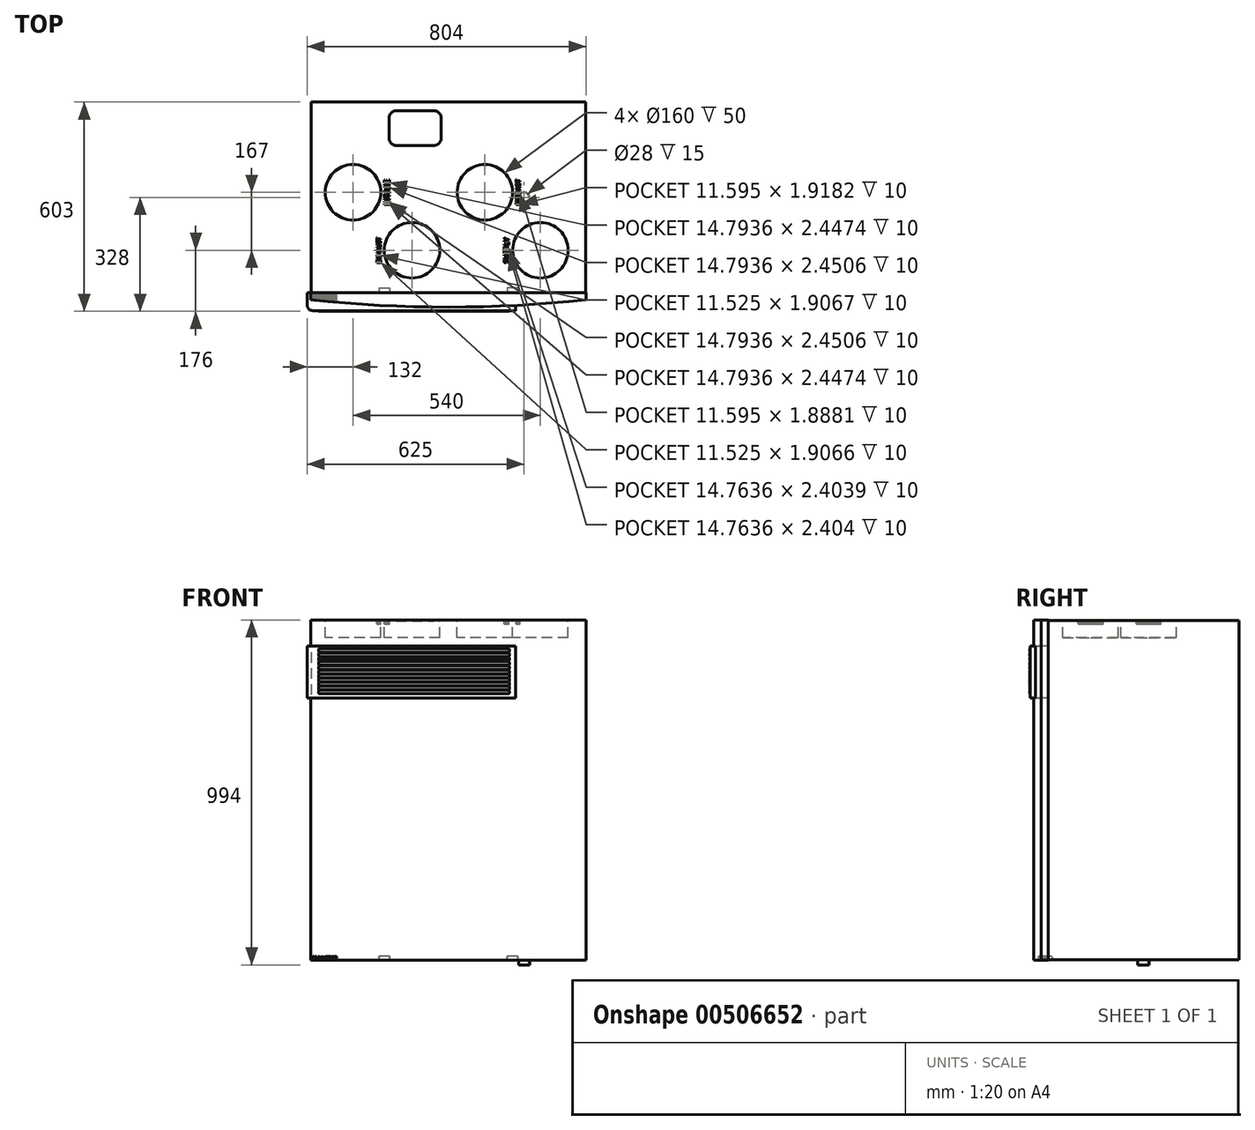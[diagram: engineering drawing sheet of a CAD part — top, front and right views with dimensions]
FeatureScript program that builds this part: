
annotation { "Feature Type Name" : "Feature", "Feature Type Description" : "" }
export const myFeature = defineFeature(function(context is Context, id is Id, definition is map)
    precondition{}
    {
        {
            var Q0;
            Q0=qCreatedBy(makeId("Top.planeOp"),FACE);
            var sketch = newSketch(context, id + "F0", { "sketchPlane" : qUnion([Q0])});
            skLineSegment(sketch, "E0", {"start": v(0, 0) * mm, "end": v(0, 275) * mm, "construction": true});
            skLineSegment(sketch, "E1", {"start": v(0, 275) * mm, "end": v(396, 275) * mm, "construction": true});
            skLineSegment(sketch, "E2.bottom", {"start": v(396, 275) * mm, "end": v(-396, 275) * mm});
            skLineSegment(sketch, "E2.top", {"start": v(396, -275) * mm, "end": v(-396, -275) * mm});
            skLineSegment(sketch, "E2.left", {"start": v(396, 275) * mm, "end": v(396, -275) * mm});
            skLineSegment(sketch, "E2.right", {"start": v(-396, 275) * mm, "end": v(-396, -275) * mm});
            skPoint(sketch, "E2.middle", {"position": v(0, 0) * mm});
            skSolve(sketch);
        }
        {
            var Q0;
            Q0 = qSketchRegion(id + "F0", true);
            extrude(context, id + "F1", {"entities" : qUnion([Q0]), "depth" : 978 * mm});
        }
        {
            var Q0;
            Q0=makeQuery(id+"F1.opExtrude","CAP_FACE",FACE,{"disambiguationData":[OSD([sQuery(id+"F0.wireOp",EDGE,"E2.bottom"),sQuery(id+"F0.wireOp",EDGE,"E2.top"),sQuery(id+"F0.wireOp",EDGE,"E2.left"),sQuery(id+"F0.wireOp",EDGE,"E2.right")])],"isStart":false});
            var sketch = newSketch(context, id + "F2", { "sketchPlane" : qUnion([Q0])});
            skLineSegment(sketch, "E3.0", {"start": v(396, -275) * mm, "end": v(-396, -275) * mm, "construction": true});
            skLineSegment(sketch, "E4", {"start": v(0, -275) * mm, "end": v(0, -316) * mm, "construction": true});
            skPoint(sketch, "E4.endSnap0", {"position": v(0, -275) * mm});
            skLineSegment(sketch, "E5", {"start": v(-396, -275) * mm, "end": v(-397, -275) * mm, "construction": true});
            skLineSegment(sketch, "E6", {"start": v(-397, -275) * mm, "end": v(-397, -295) * mm});
            skLineSegment(sketch, "E7", {"start": v(0, -316) * mm, "end": v(-397, -295) * mm, "construction": true});
            skLineSegment(sketch, "E8", {"start": v(-198.5, -305.5) * mm, "end": v(0, 3447.1) * mm, "construction": true});
            skLineSegment(sketch, "E9", {"start": v(0, -316) * mm, "end": v(0, 3447.1) * mm, "construction": true});
            skArc(sketch, "E10", {"start": v(-397, -295) * mm, "mid": v(0, -316) * mm, "end": v(397, -295) * mm});
            skLineSegment(sketch, "E11.MirrorCS", {"start": v(397, -275) * mm, "end": v(397, -295) * mm});
            skLineSegment(sketch, "E12.MirrorCS", {"start": v(396, -275) * mm, "end": v(397, -275) * mm, "construction": true});
            skLineSegment(sketch, "E13", {"start": v(-397, -275) * mm, "end": v(397, -275) * mm});
            skSolve(sketch);
        }
        {
            var Q0;
            {var subQ2=sQuery(id+"F2.wireOp",EDGE,"E6");Q0=makeQuery(id+"F2.imprint","IMPRINT",FACE,{"disambiguationData":[TD([[makeQuery(id+"F2.imprint","IMPRINT",EDGE,{"derivedFrom":subQ2}),1.0]])]});}
            var Q1;
            Q1=makeQuery(id+"F1.opExtrude","CAP_FACE",FACE,{"disambiguationData":[OSD([sQuery(id+"F0.wireOp",EDGE,"E2.bottom"),sQuery(id+"F0.wireOp",EDGE,"E2.top"),sQuery(id+"F0.wireOp",EDGE,"E2.left"),sQuery(id+"F0.wireOp",EDGE,"E2.right")])],"isStart":true});
            extrude(context, id + "F3", {"entities" : qUnion([Q0]), "operationType" : NewBodyOperationType.ADD, "endBound" : BoundingType.UP_TO_SURFACE, "oppositeDirection" : true, "endBoundEntityFace" : qUnion([Q1]), "depth" : 25 * mm, "hasSecondDirection" : true, "secondDirectionOppositeDirection" : false, "secondDirectionDepth" : 1 * mm});
        }
        {
            var Q0;
            Q0=makeQuery(id+"F1.opExtrude","CAP_FACE",FACE,{"disambiguationData":[OSD([sQuery(id+"F0.wireOp",EDGE,"E2.bottom"),sQuery(id+"F0.wireOp",EDGE,"E2.top"),sQuery(id+"F0.wireOp",EDGE,"E2.left"),sQuery(id+"F0.wireOp",EDGE,"E2.right")])],"isStart":false});
            var sketch = newSketch(context, id + "F4", { "sketchPlane" : qUnion([Q0])});
            skLineSegment(sketch, "E14", {"start": v(-396, 275) * mm, "end": v(-105, 275) * mm, "construction": true});
            skLineSegment(sketch, "E15", {"start": v(-105, 275) * mm, "end": v(-105, -152) * mm, "construction": true});
            skLineSegment(sketch, "E16", {"start": v(-396, 275) * mm, "end": v(-275, 275) * mm, "construction": true});
            skLineSegment(sketch, "E17", {"start": v(-275, 275) * mm, "end": v(-275, 15) * mm, "construction": true});
            skCircle(sketch, "E18", {"center": v(-275, 15) * mm, "radius": 80 * mm});
            skCircle(sketch, "E19", {"center": v(-105, -152) * mm, "radius": 80 * mm});
            skLineSegment(sketch, "E20", {"start": v(396, 275) * mm, "end": v(105, 275) * mm, "construction": true});
            skLineSegment(sketch, "E21", {"start": v(105, 275) * mm, "end": v(105, 15) * mm, "construction": true});
            skLineSegment(sketch, "E22", {"start": v(396, 275) * mm, "end": v(265, 275) * mm, "construction": true});
            skLineSegment(sketch, "E23", {"start": v(265, 275) * mm, "end": v(265, -152) * mm, "construction": true});
            skCircle(sketch, "E24", {"center": v(265, -152) * mm, "radius": 80 * mm});
            skCircle(sketch, "E25", {"center": v(105, 15) * mm, "radius": 80 * mm});
            skSolve(sketch);
        }
        {
            var Q0;
            Q0 = qSketchRegion(id + "F4", true);
            extrude(context, id + "F5", {"entities" : qUnion([Q0]), "operationType" : NewBodyOperationType.REMOVE, "oppositeDirection" : true, "depth" : 50 * mm});
        }
        {
            var Q0;
            Q0=makeQuery(id+"F1.opExtrude","CAP_FACE",FACE,{"disambiguationData":[OSD([sQuery(id+"F0.wireOp",EDGE,"E2.bottom"),sQuery(id+"F0.wireOp",EDGE,"E2.top"),sQuery(id+"F0.wireOp",EDGE,"E2.left"),sQuery(id+"F0.wireOp",EDGE,"E2.right")])],"isStart":false});
            var sketch = newSketch(context, id + "F6", { "sketchPlane" : qUnion([Q0])});
            skLineSegment(sketch, "E26", {"start": v(-396, 200) * mm, "end": v(-96, 200) * mm, "construction": true});
            skLineSegment(sketch, "E27.bottom", {"start": v(-151, 250) * mm, "end": v(-41, 250) * mm});
            skLineSegment(sketch, "E27.top", {"start": v(-151, 150) * mm, "end": v(-41, 150) * mm});
            skLineSegment(sketch, "E27.left", {"start": v(-171, 230) * mm, "end": v(-171, 170) * mm});
            skLineSegment(sketch, "E27.right", {"start": v(-21, 230) * mm, "end": v(-21, 170) * mm});
            skPoint(sketch, "E27.middle", {"position": v(-96, 200) * mm});
            skPoint(sketch, "E28.visualSharp", {"position": v(-171, 250) * mm});
            skArc(sketch, "E28.filletArc", {"start": v(-151, 250) * mm, "mid": v(-165.14, 244.14) * mm, "end": v(-171, 230) * mm});
            skPoint(sketch, "E29.visualSharp", {"position": v(-21, 250) * mm});
            skArc(sketch, "E29.filletArc", {"start": v(-21, 230) * mm, "mid": v(-26.86, 244.14) * mm, "end": v(-41, 250) * mm});
            skPoint(sketch, "E30.visualSharp", {"position": v(-21, 150) * mm});
            skArc(sketch, "E30.filletArc", {"start": v(-41, 150) * mm, "mid": v(-26.86, 155.86) * mm, "end": v(-21, 170) * mm});
            skPoint(sketch, "E31.visualSharp", {"position": v(-171, 150) * mm});
            skArc(sketch, "E31.filletArc", {"start": v(-171, 170) * mm, "mid": v(-165.14, 155.86) * mm, "end": v(-151, 150) * mm});
            skSolve(sketch);
        }
        {
            var Q0;
            Q0 = qSketchRegion(id + "F6", true);
            var Q1;
            Q1 = qConstructionFilter(qBodyType(qCreatedBy(id + "F6" ,EDGE), BodyType.WIRE), ConstructionObject.NO);
            extrude(context, id + "F7", {"entities" : qUnion([Q0]), "operationType" : NewBodyOperationType.REMOVE, "surfaceEntities" : qUnion([Q1]), "oppositeDirection" : true, "depth" : 2 * mm});
        }
        {
            var Q0;
            Q0=makeQuery(id+"F3.opExtrude","CAP_EDGE",EDGE,{"disambiguationData":[OSD([sQuery(id+"F2.wireOp",EDGE,"E10")])],"isStart":true});
            cPoint(context, id + "F8", {"entities" : qUnion([Q0]), "parameter" : 0.5});
        }
        {
            var Q0;
            Q0=qCreatedBy(makeId("Front.planeOp"),FACE);
            var Q1;
            Q1 = qCreatedBy(id + "F8" ,VERTEX);
            cPlane(context, id + "F9", {"entities" : qUnion([Q0, Q1]), "cplaneType" : CPlaneType.PLANE_POINT, "offset" : 200 * mm, "oppositeDirection" : true, "width" : 150 * mm, "height" : 150 * mm});
        }
        {
            var Q0;
            Q0=qCreatedBy(id+"F9.planeOp",FACE);
            cPlane(context, id + "F10", {"entities" : qUnion([Q0]), "cplaneType" : CPlaneType.OFFSET, "offset" : 10 * mm, "width" : 150 * mm, "height" : 150 * mm});
        }
        {
            var Q0;
            Q0=qCreatedBy(id+"F10.planeOp",FACE);
            var sketch = newSketch(context, id + "F11", { "sketchPlane" : qUnion([Q0])});
            skLineSegment(sketch, "E32.0", {"start": v(-397, 979) * mm, "end": v(397, 979) * mm, "construction": true});
            skLineSegment(sketch, "E33.bottom", {"start": v(-407, 904) * mm, "end": v(193, 904) * mm});
            skLineSegment(sketch, "E33.top", {"start": v(-407, 754) * mm, "end": v(193, 754) * mm});
            skLineSegment(sketch, "E33.left", {"start": v(-407, 904) * mm, "end": v(-407, 754) * mm});
            skLineSegment(sketch, "E33.right", {"start": v(193, 904) * mm, "end": v(193, 754) * mm});
            skLineSegment(sketch, "E34", {"start": v(-397, 979) * mm, "end": v(-407, 979) * mm});
            skLineSegment(sketch, "E35", {"start": v(-407, 979) * mm, "end": v(-407, 904) * mm, "construction": true});
            skSolve(sketch);
        }
        {
            var Q0;
            Q0=makeQuery(id+"F11.imprint","IMPRINT",FACE,{"disambiguationData":[TD([[makeQuery(id+"F11.imprint","IMPRINT",EDGE,{"derivedFrom":sQuery(id+"F11.wireOp",EDGE,"E33.bottom")}),-1.0]])]});
            var Q1;
            Q1=makeQuery(id+"F3.opExtrude","SWEPT_FACE",FACE,{"disambiguationData":[OSD([sQuery(id+"F2.wireOp",EDGE,"E13")])]});
            extrude(context, id + "F12", {"entities" : qUnion([Q0]), "operationType" : NewBodyOperationType.ADD, "endBound" : BoundingType.UP_TO_SURFACE, "oppositeDirection" : true, "endBoundEntityFace" : qUnion([Q1]), "depth" : 25 * mm});
        }
        {
            var Q0;
            Q0=makeQuery(id+"F12.opExtrude","CAP_EDGE",EDGE,{"disambiguationData":[OSD([sQuery(id+"F11.wireOp",EDGE,"E33.left")])],"isStart":true});
            fillet(context, id + "F13", {"entities" : qUnion([Q0]), "radius" : 15 * mm, "tangentPropagation" : true, "allowEdgeOverflow" : false});
        }
        {
            var Q0;
            Q0=makeQuery(id+"F1.opExtrude","CAP_FACE",FACE,{"disambiguationData":[OSD([sQuery(id+"F0.wireOp",EDGE,"E2.bottom"),sQuery(id+"F0.wireOp",EDGE,"E2.top"),sQuery(id+"F0.wireOp",EDGE,"E2.left"),sQuery(id+"F0.wireOp",EDGE,"E2.right")])],"isStart":false});
            var sketch = newSketch(context, id + "F14", { "sketchPlane" : qUnion([Q0])});
            skCircle(sketch, "E36.0", {"center": v(105, 15) * mm, "radius": 80 * mm, "construction": true});
            skCircle(sketch, "E36.1", {"center": v(265, -152) * mm, "radius": 80 * mm, "construction": true});
            skCircle(sketch, "E36.2", {"center": v(-105, -152) * mm, "radius": 80 * mm, "construction": true});
            skCircle(sketch, "E36.3", {"center": v(-275, 15) * mm, "radius": 80 * mm, "construction": true});
            skLineSegment(sketch, "E37", {"start": v(105, 15) * mm, "end": v(195, 15) * mm, "construction": true});
            skText(sketch, "E38", { "text": "EXTRACT", "fontName": "AllertaStencil-Regular.ttf"});
            skLineSegment(sketch, "E39", {"start": v(265, -152) * mm, "end": v(175, -152) * mm, "construction": true});
            skText(sketch, "E40", { "text": "SUPPLY", "fontName": "AllertaStencil-Regular.ttf"});
            skLineSegment(sketch, "E41", {"start": v(-105, -152) * mm, "end": v(-195, -152) * mm, "construction": true});
            skText(sketch, "E42", { "text": "EXHAUST", "fontName": "AllertaStencil-Regular.ttf"});
            skLineSegment(sketch, "E43", {"start": v(-275, 15) * mm, "end": v(-185, 15) * mm, "construction": true});
            skText(sketch, "E44", { "text": "INTAKE ", "fontName": "AllertaStencil-Regular.ttf"});
            const initialGuessF14  = {"E38": [0.2066, -0.0225, 0, 1, 0.0116], "E40": [0.175, -0.1895, 0, 1, 0.01477], "E42": [-0.195, -0.1895, 0, 1, 0.01153], "E44": [-0.1702, -0.0225, 0, 1, 0.0148]};
            skSetInitialGuess(sketch, initialGuessF14);
            skSolve(sketch);
        }
        {
            var Q0;
            Q0 = qSketchRegion(id + "F14", true);
            extrude(context, id + "F15", {"entities" : qUnion([Q0]), "operationType" : NewBodyOperationType.REMOVE, "oppositeDirection" : true, "depth" : 10 * mm});
        }
        {
            var Q0;
            Q0=makeQuery(id+"F12.opExtrude","CAP_FACE",FACE,{"disambiguationData":[OSD([sQuery(id+"F11.wireOp",EDGE,"E33.bottom"),sQuery(id+"F11.wireOp",EDGE,"E33.top"),sQuery(id+"F11.wireOp",EDGE,"E33.left"),sQuery(id+"F11.wireOp",EDGE,"E33.right")])],"isStart":true});
            var sketch = newSketch(context, id + "F16", { "sketchPlane" : qUnion([Q0])});
            skLineSegment(sketch, "E45", {"start": v(193, 829) * mm, "end": v(-392, 829) * mm, "construction": true});
            skLineSegment(sketch, "E46.bottom", {"start": v(-372, 834) * mm, "end": v(173, 834) * mm});
            skLineSegment(sketch, "E46.top", {"start": v(-372, 824) * mm, "end": v(173, 824) * mm});
            skLineSegment(sketch, "E46.left", {"start": v(-374.5, 831.5) * mm, "end": v(-374.5, 826.5) * mm});
            skLineSegment(sketch, "E46.right", {"start": v(175.5, 831.5) * mm, "end": v(175.5, 826.5) * mm});
            skPoint(sketch, "E46.middle", {"position": v(-99.5, 829) * mm});
            skPoint(sketch, "E47.visualSharp", {"position": v(-374.5, 834) * mm});
            skArc(sketch, "E47.filletArc", {"start": v(-372, 834) * mm, "mid": v(-373.77, 833.27) * mm, "end": v(-374.5, 831.5) * mm});
            skPoint(sketch, "E48.visualSharp", {"position": v(-374.5, 824) * mm});
            skArc(sketch, "E48.filletArc", {"start": v(-374.5, 826.5) * mm, "mid": v(-373.77, 824.73) * mm, "end": v(-372, 824) * mm});
            skPoint(sketch, "E49.visualSharp", {"position": v(175.5, 824) * mm});
            skArc(sketch, "E49.filletArc", {"start": v(173, 824) * mm, "mid": v(174.77, 824.73) * mm, "end": v(175.5, 826.5) * mm});
            skPoint(sketch, "E50.visualSharp", {"position": v(175.5, 834) * mm});
            skArc(sketch, "E50.filletArc", {"start": v(175.5, 831.5) * mm, "mid": v(174.77, 833.27) * mm, "end": v(173, 834) * mm});
            skArc(sketch, "E51.0.1.0", {"start": v(-374.5, 839) * mm, "mid": v(-373.77, 837.23) * mm, "end": v(-372, 836.5) * mm});
            skLineSegment(sketch, "E51.0.1.1", {"start": v(-374.5, 844) * mm, "end": v(-374.5, 839) * mm});
            skArc(sketch, "E51.0.1.2", {"start": v(-372, 846.5) * mm, "mid": v(-373.77, 845.77) * mm, "end": v(-374.5, 844) * mm});
            skLineSegment(sketch, "E51.0.1.3", {"start": v(-372, 846.5) * mm, "end": v(173, 846.5) * mm});
            skLineSegment(sketch, "E51.0.1.4", {"start": v(-372, 836.5) * mm, "end": v(173, 836.5) * mm});
            skArc(sketch, "E51.0.1.5", {"start": v(173, 836.5) * mm, "mid": v(174.77, 837.23) * mm, "end": v(175.5, 839) * mm});
            skLineSegment(sketch, "E51.0.1.6", {"start": v(175.5, 844) * mm, "end": v(175.5, 839) * mm});
            skArc(sketch, "E51.0.1.7", {"start": v(175.5, 844) * mm, "mid": v(174.77, 845.77) * mm, "end": v(173, 846.5) * mm});
            skArc(sketch, "E51.0.2.0", {"start": v(-374.5, 851.5) * mm, "mid": v(-373.77, 849.73) * mm, "end": v(-372, 849) * mm});
            skLineSegment(sketch, "E51.0.2.1", {"start": v(-374.5, 856.5) * mm, "end": v(-374.5, 851.5) * mm});
            skArc(sketch, "E51.0.2.2", {"start": v(-372, 859) * mm, "mid": v(-373.77, 858.27) * mm, "end": v(-374.5, 856.5) * mm});
            skLineSegment(sketch, "E51.0.2.3", {"start": v(-372, 859) * mm, "end": v(173, 859) * mm});
            skLineSegment(sketch, "E51.0.2.4", {"start": v(-372, 849) * mm, "end": v(173, 849) * mm});
            skArc(sketch, "E51.0.2.5", {"start": v(173, 849) * mm, "mid": v(174.77, 849.73) * mm, "end": v(175.5, 851.5) * mm});
            skLineSegment(sketch, "E51.0.2.6", {"start": v(175.5, 856.5) * mm, "end": v(175.5, 851.5) * mm});
            skArc(sketch, "E51.0.2.7", {"start": v(175.5, 856.5) * mm, "mid": v(174.77, 858.27) * mm, "end": v(173, 859) * mm});
            skArc(sketch, "E51.0.3.0", {"start": v(-374.5, 864) * mm, "mid": v(-373.77, 862.23) * mm, "end": v(-372, 861.5) * mm});
            skLineSegment(sketch, "E51.0.3.1", {"start": v(-374.5, 869) * mm, "end": v(-374.5, 864) * mm});
            skArc(sketch, "E51.0.3.2", {"start": v(-372, 871.5) * mm, "mid": v(-373.77, 870.77) * mm, "end": v(-374.5, 869) * mm});
            skLineSegment(sketch, "E51.0.3.3", {"start": v(-372, 871.5) * mm, "end": v(173, 871.5) * mm});
            skLineSegment(sketch, "E51.0.3.4", {"start": v(-372, 861.5) * mm, "end": v(173, 861.5) * mm});
            skArc(sketch, "E51.0.3.5", {"start": v(173, 861.5) * mm, "mid": v(174.77, 862.23) * mm, "end": v(175.5, 864) * mm});
            skLineSegment(sketch, "E51.0.3.6", {"start": v(175.5, 869) * mm, "end": v(175.5, 864) * mm});
            skArc(sketch, "E51.0.3.7", {"start": v(175.5, 869) * mm, "mid": v(174.77, 870.77) * mm, "end": v(173, 871.5) * mm});
            skArc(sketch, "E51.0.4.0", {"start": v(-374.5, 876.5) * mm, "mid": v(-373.77, 874.73) * mm, "end": v(-372, 874) * mm});
            skLineSegment(sketch, "E51.0.4.1", {"start": v(-374.5, 881.5) * mm, "end": v(-374.5, 876.5) * mm});
            skArc(sketch, "E51.0.4.2", {"start": v(-372, 884) * mm, "mid": v(-373.77, 883.27) * mm, "end": v(-374.5, 881.5) * mm});
            skLineSegment(sketch, "E51.0.4.3", {"start": v(-372, 884) * mm, "end": v(173, 884) * mm});
            skLineSegment(sketch, "E51.0.4.4", {"start": v(-372, 874) * mm, "end": v(173, 874) * mm});
            skArc(sketch, "E51.0.4.5", {"start": v(173, 874) * mm, "mid": v(174.77, 874.73) * mm, "end": v(175.5, 876.5) * mm});
            skLineSegment(sketch, "E51.0.4.6", {"start": v(175.5, 881.5) * mm, "end": v(175.5, 876.5) * mm});
            skArc(sketch, "E51.0.4.7", {"start": v(175.5, 881.5) * mm, "mid": v(174.77, 883.27) * mm, "end": v(173, 884) * mm});
            skArc(sketch, "E51.0.5.0", {"start": v(-374.5, 889) * mm, "mid": v(-373.77, 887.23) * mm, "end": v(-372, 886.5) * mm});
            skLineSegment(sketch, "E51.0.5.1", {"start": v(-374.5, 894) * mm, "end": v(-374.5, 889) * mm});
            skArc(sketch, "E51.0.5.2", {"start": v(-372, 896.5) * mm, "mid": v(-373.77, 895.77) * mm, "end": v(-374.5, 894) * mm});
            skLineSegment(sketch, "E51.0.5.3", {"start": v(-372, 896.5) * mm, "end": v(173, 896.5) * mm});
            skLineSegment(sketch, "E51.0.5.4", {"start": v(-372, 886.5) * mm, "end": v(173, 886.5) * mm});
            skArc(sketch, "E51.0.5.5", {"start": v(173, 886.5) * mm, "mid": v(174.77, 887.23) * mm, "end": v(175.5, 889) * mm});
            skLineSegment(sketch, "E51.0.5.6", {"start": v(175.5, 894) * mm, "end": v(175.5, 889) * mm});
            skArc(sketch, "E51.0.5.7", {"start": v(175.5, 894) * mm, "mid": v(174.77, 895.77) * mm, "end": v(173, 896.5) * mm});
            skLineSegment(sketch, "E51.direction1", {"start": v(-372, 824) * mm, "end": v(-362.5, 824) * mm, "construction": true});
            skLineSegment(sketch, "E51.direction2", {"start": v(-372, 824) * mm, "end": v(-372, 836.5) * mm, "construction": true});
            skSolve(sketch);
        }
        {
            var Q0;
            Q0=makeQuery(id+"F16.imprint","IMPRINT",FACE,{"disambiguationData":[TD([[makeQuery(id+"F16.imprint","IMPRINT",EDGE,{"derivedFrom":sQuery(id+"F16.wireOp",EDGE,"E46.bottom")}),-1.0]])]});
            var Q1;
            Q1=makeQuery(id+"F16.imprint","IMPRINT",FACE,{"disambiguationData":[TD([[makeQuery(id+"F16.imprint","IMPRINT",EDGE,{"derivedFrom":sQuery(id+"F16.wireOp",EDGE,"E51.0.1.0")}),1.0]])]});
            var Q2;
            Q2=makeQuery(id+"F16.imprint","IMPRINT",FACE,{"disambiguationData":[TD([[makeQuery(id+"F16.imprint","IMPRINT",EDGE,{"derivedFrom":sQuery(id+"F16.wireOp",EDGE,"E51.0.2.0")}),1.0]])]});
            var Q3;
            Q3=makeQuery(id+"F16.imprint","IMPRINT",FACE,{"disambiguationData":[TD([[makeQuery(id+"F16.imprint","IMPRINT",EDGE,{"derivedFrom":sQuery(id+"F16.wireOp",EDGE,"E51.0.3.0")}),1.0]])]});
            var Q4;
            Q4=makeQuery(id+"F16.imprint","IMPRINT",FACE,{"disambiguationData":[TD([[makeQuery(id+"F16.imprint","IMPRINT",EDGE,{"derivedFrom":sQuery(id+"F16.wireOp",EDGE,"E51.0.4.0")}),1.0]])]});
            var Q5;
            Q5=makeQuery(id+"F16.imprint","IMPRINT",FACE,{"disambiguationData":[TD([[makeQuery(id+"F16.imprint","IMPRINT",EDGE,{"derivedFrom":sQuery(id+"F16.wireOp",EDGE,"E51.0.5.0")}),1.0]])]});
            extrude(context, id + "F17", {"entities" : qUnion([Q0, Q1, Q2, Q3, Q4, Q5]), "operationType" : NewBodyOperationType.ADD, "depth" : 2 * mm});
        }
        {
            var Q0;
            Q0=makeQuery(id+"F12.opExtrude","CAP_FACE",FACE,{"disambiguationData":[OSD([sQuery(id+"F11.wireOp",EDGE,"E33.bottom"),sQuery(id+"F11.wireOp",EDGE,"E33.top"),sQuery(id+"F11.wireOp",EDGE,"E33.left"),sQuery(id+"F11.wireOp",EDGE,"E33.right")])],"isStart":true});
            var sketch = newSketch(context, id + "F18", { "sketchPlane" : qUnion([Q0])});
            skArc(sketch, "E52.0.0", {"start": v(-374.5, 826.5) * mm, "mid": v(-373.77, 824.73) * mm, "end": v(-372, 824) * mm});
            skLineSegment(sketch, "E52.0.1", {"start": v(-372, 824) * mm, "end": v(173, 824) * mm});
            skArc(sketch, "E52.0.2", {"start": v(173, 824) * mm, "mid": v(174.77, 824.73) * mm, "end": v(175.5, 826.5) * mm});
            skLineSegment(sketch, "E52.0.3", {"start": v(175.5, 826.5) * mm, "end": v(175.5, 831.5) * mm});
            skArc(sketch, "E52.0.4", {"start": v(175.5, 831.5) * mm, "mid": v(174.77, 833.27) * mm, "end": v(173, 834) * mm});
            skLineSegment(sketch, "E52.0.5", {"start": v(173, 834) * mm, "end": v(-372, 834) * mm});
            skArc(sketch, "E52.0.6", {"start": v(-372, 834) * mm, "mid": v(-373.77, 833.27) * mm, "end": v(-374.5, 831.5) * mm});
            skLineSegment(sketch, "E52.0.7", {"start": v(-374.5, 831.5) * mm, "end": v(-374.5, 826.5) * mm});
            skLineSegment(sketch, "E53.0.1.0", {"start": v(-372, 812.5) * mm, "end": v(173, 812.5) * mm});
            skArc(sketch, "E53.0.1.1", {"start": v(-374.5, 815) * mm, "mid": v(-373.77, 813.23) * mm, "end": v(-372, 812.5) * mm});
            skLineSegment(sketch, "E53.0.1.2", {"start": v(-374.5, 820) * mm, "end": v(-374.5, 815) * mm});
            skArc(sketch, "E53.0.1.3", {"start": v(-372, 822.5) * mm, "mid": v(-373.77, 821.77) * mm, "end": v(-374.5, 820) * mm});
            skLineSegment(sketch, "E53.0.1.4", {"start": v(173, 822.5) * mm, "end": v(-372, 822.5) * mm});
            skArc(sketch, "E53.0.1.5", {"start": v(173, 812.5) * mm, "mid": v(174.77, 813.23) * mm, "end": v(175.5, 815) * mm});
            skArc(sketch, "E53.0.1.6", {"start": v(175.5, 820) * mm, "mid": v(174.77, 821.77) * mm, "end": v(173, 822.5) * mm});
            skLineSegment(sketch, "E53.0.1.7", {"start": v(175.5, 815) * mm, "end": v(175.5, 820) * mm});
            skLineSegment(sketch, "E53.0.2.0", {"start": v(-372, 801) * mm, "end": v(173, 801) * mm});
            skArc(sketch, "E53.0.2.1", {"start": v(-374.5, 803.5) * mm, "mid": v(-373.77, 801.73) * mm, "end": v(-372, 801) * mm});
            skLineSegment(sketch, "E53.0.2.2", {"start": v(-374.5, 808.5) * mm, "end": v(-374.5, 803.5) * mm});
            skArc(sketch, "E53.0.2.3", {"start": v(-372, 811) * mm, "mid": v(-373.77, 810.27) * mm, "end": v(-374.5, 808.5) * mm});
            skLineSegment(sketch, "E53.0.2.4", {"start": v(173, 811) * mm, "end": v(-372, 811) * mm});
            skArc(sketch, "E53.0.2.5", {"start": v(173, 801) * mm, "mid": v(174.77, 801.73) * mm, "end": v(175.5, 803.5) * mm});
            skArc(sketch, "E53.0.2.6", {"start": v(175.5, 808.5) * mm, "mid": v(174.77, 810.27) * mm, "end": v(173, 811) * mm});
            skLineSegment(sketch, "E53.0.2.7", {"start": v(175.5, 803.5) * mm, "end": v(175.5, 808.5) * mm});
            skLineSegment(sketch, "E53.0.3.0", {"start": v(-372, 789.5) * mm, "end": v(173, 789.5) * mm});
            skArc(sketch, "E53.0.3.1", {"start": v(-374.5, 792) * mm, "mid": v(-373.77, 790.23) * mm, "end": v(-372, 789.5) * mm});
            skLineSegment(sketch, "E53.0.3.2", {"start": v(-374.5, 797) * mm, "end": v(-374.5, 792) * mm});
            skArc(sketch, "E53.0.3.3", {"start": v(-372, 799.5) * mm, "mid": v(-373.77, 798.77) * mm, "end": v(-374.5, 797) * mm});
            skLineSegment(sketch, "E53.0.3.4", {"start": v(173, 799.5) * mm, "end": v(-372, 799.5) * mm});
            skArc(sketch, "E53.0.3.5", {"start": v(173, 789.5) * mm, "mid": v(174.77, 790.23) * mm, "end": v(175.5, 792) * mm});
            skArc(sketch, "E53.0.3.6", {"start": v(175.5, 797) * mm, "mid": v(174.77, 798.77) * mm, "end": v(173, 799.5) * mm});
            skLineSegment(sketch, "E53.0.3.7", {"start": v(175.5, 792) * mm, "end": v(175.5, 797) * mm});
            skLineSegment(sketch, "E53.0.4.0", {"start": v(-372, 778) * mm, "end": v(173, 778) * mm});
            skArc(sketch, "E53.0.4.1", {"start": v(-374.5, 780.5) * mm, "mid": v(-373.77, 778.73) * mm, "end": v(-372, 778) * mm});
            skLineSegment(sketch, "E53.0.4.2", {"start": v(-374.5, 785.5) * mm, "end": v(-374.5, 780.5) * mm});
            skArc(sketch, "E53.0.4.3", {"start": v(-372, 788) * mm, "mid": v(-373.77, 787.27) * mm, "end": v(-374.5, 785.5) * mm});
            skLineSegment(sketch, "E53.0.4.4", {"start": v(173, 788) * mm, "end": v(-372, 788) * mm});
            skArc(sketch, "E53.0.4.5", {"start": v(173, 778) * mm, "mid": v(174.77, 778.73) * mm, "end": v(175.5, 780.5) * mm});
            skArc(sketch, "E53.0.4.6", {"start": v(175.5, 785.5) * mm, "mid": v(174.77, 787.27) * mm, "end": v(173, 788) * mm});
            skLineSegment(sketch, "E53.0.4.7", {"start": v(175.5, 780.5) * mm, "end": v(175.5, 785.5) * mm});
            skLineSegment(sketch, "E53.0.5.0", {"start": v(-372, 766.5) * mm, "end": v(173, 766.5) * mm});
            skArc(sketch, "E53.0.5.1", {"start": v(-374.5, 769) * mm, "mid": v(-373.77, 767.23) * mm, "end": v(-372, 766.5) * mm});
            skLineSegment(sketch, "E53.0.5.2", {"start": v(-374.5, 774) * mm, "end": v(-374.5, 769) * mm});
            skArc(sketch, "E53.0.5.3", {"start": v(-372, 776.5) * mm, "mid": v(-373.77, 775.77) * mm, "end": v(-374.5, 774) * mm});
            skLineSegment(sketch, "E53.0.5.4", {"start": v(173, 776.5) * mm, "end": v(-372, 776.5) * mm});
            skArc(sketch, "E53.0.5.5", {"start": v(173, 766.5) * mm, "mid": v(174.77, 767.23) * mm, "end": v(175.5, 769) * mm});
            skArc(sketch, "E53.0.5.6", {"start": v(175.5, 774) * mm, "mid": v(174.77, 775.77) * mm, "end": v(173, 776.5) * mm});
            skLineSegment(sketch, "E53.0.5.7", {"start": v(175.5, 769) * mm, "end": v(175.5, 774) * mm});
            skLineSegment(sketch, "E53.direction1", {"start": v(-372, 824) * mm, "end": v(-347, 824) * mm, "construction": true});
            skLineSegment(sketch, "E53.direction2", {"start": v(-372, 824) * mm, "end": v(-372, 812.5) * mm, "construction": true});
            skSolve(sketch);
        }
        {
            var Q0;
            Q0=makeQuery(id+"F18.imprint","IMPRINT",FACE,{"disambiguationData":[TD([[makeQuery(id+"F18.imprint","IMPRINT",EDGE,{"derivedFrom":sQuery(id+"F18.wireOp",EDGE,"E52.0.0")}),1.0]])]});
            var Q1;
            Q1=makeQuery(id+"F18.imprint","IMPRINT",FACE,{"disambiguationData":[TD([[makeQuery(id+"F18.imprint","IMPRINT",EDGE,{"derivedFrom":sQuery(id+"F18.wireOp",EDGE,"E53.0.1.0")}),1.0]])]});
            var Q2;
            Q2=makeQuery(id+"F18.imprint","IMPRINT",FACE,{"disambiguationData":[TD([[makeQuery(id+"F18.imprint","IMPRINT",EDGE,{"derivedFrom":sQuery(id+"F18.wireOp",EDGE,"E53.0.2.0")}),1.0]])]});
            var Q3;
            Q3=makeQuery(id+"F18.imprint","IMPRINT",FACE,{"disambiguationData":[TD([[makeQuery(id+"F18.imprint","IMPRINT",EDGE,{"derivedFrom":sQuery(id+"F18.wireOp",EDGE,"E53.0.3.0")}),1.0]])]});
            var Q4;
            Q4=makeQuery(id+"F18.imprint","IMPRINT",FACE,{"disambiguationData":[TD([[makeQuery(id+"F18.imprint","IMPRINT",EDGE,{"derivedFrom":sQuery(id+"F18.wireOp",EDGE,"E53.0.5.0")}),1.0]])]});
            var Q5;
            Q5=makeQuery(id+"F18.imprint","IMPRINT",FACE,{"disambiguationData":[TD([[makeQuery(id+"F18.imprint","IMPRINT",EDGE,{"derivedFrom":sQuery(id+"F18.wireOp",EDGE,"E53.0.4.0")}),1.0]])]});
            extrude(context, id + "F19", {"entities" : qUnion([Q0, Q1, Q2, Q3, Q4, Q5]), "operationType" : NewBodyOperationType.ADD, "depth" : 2 * mm});
        }
        {
            var Q0;
            Q0=makeQuery(id+"F17.opExtrude","CAP_EDGE",EDGE,{"disambiguationData":[OSD([sQuery(id+"F16.wireOp",EDGE,"E51.0.5.1")])],"isStart":false});
            var Q1;
            Q1=makeQuery(id+"F17.opExtrude","CAP_EDGE",EDGE,{"disambiguationData":[OSD([sQuery(id+"F16.wireOp",EDGE,"E51.0.4.1")])],"isStart":false});
            var Q2;
            Q2=makeQuery(id+"F17.opExtrude","CAP_EDGE",EDGE,{"disambiguationData":[OSD([sQuery(id+"F16.wireOp",EDGE,"E51.0.3.1")])],"isStart":false});
            var Q3;
            Q3=makeQuery(id+"F17.opExtrude","CAP_EDGE",EDGE,{"disambiguationData":[OSD([sQuery(id+"F16.wireOp",EDGE,"E51.0.2.1")])],"isStart":false});
            var Q4;
            Q4=makeQuery(id+"F17.opExtrude","CAP_EDGE",EDGE,{"disambiguationData":[OSD([sQuery(id+"F16.wireOp",EDGE,"E51.0.1.1")])],"isStart":false});
            var Q5;
            Q5=makeQuery(id+"F17.opExtrude","CAP_EDGE",EDGE,{"disambiguationData":[OSD([sQuery(id+"F16.wireOp",EDGE,"E46.left")])],"isStart":false});
            var Q6;
            Q6=makeQuery(id+"F19.opExtrude","CAP_EDGE",EDGE,{"disambiguationData":[OSD([sQuery(id+"F18.wireOp",EDGE,"E53.0.1.2")])],"isStart":false});
            var Q7;
            Q7=makeQuery(id+"F19.opExtrude","CAP_EDGE",EDGE,{"disambiguationData":[OSD([sQuery(id+"F18.wireOp",EDGE,"E53.0.2.2")])],"isStart":false});
            var Q8;
            Q8=makeQuery(id+"F19.opExtrude","CAP_EDGE",EDGE,{"disambiguationData":[OSD([sQuery(id+"F18.wireOp",EDGE,"E53.0.3.2")])],"isStart":false});
            var Q9;
            Q9=makeQuery(id+"F19.opExtrude","CAP_EDGE",EDGE,{"disambiguationData":[OSD([sQuery(id+"F18.wireOp",EDGE,"E53.0.4.2")])],"isStart":false});
            var Q10;
            Q10=makeQuery(id+"F19.opExtrude","CAP_EDGE",EDGE,{"disambiguationData":[OSD([sQuery(id+"F18.wireOp",EDGE,"E53.0.5.2")])],"isStart":false});
            fillet(context, id + "F20", {"entities" : qUnion([Q0, Q1, Q2, Q3, Q4, Q5, Q6, Q7, Q8, Q9, Q10]), "radius" : 2 * mm, "tangentPropagation" : true, "allowEdgeOverflow" : false});
        }
        {
            var Q0;
            {var subQ0=sQuery(id+"F0.wireOp",EDGE,"E2.right");var subQ1=sQuery(id+"F0.wireOp",EDGE,"E2.left");var subQ2=sQuery(id+"F0.wireOp",EDGE,"E2.top");var subQ3=sQuery(id+"F0.wireOp",EDGE,"E2.bottom");Q0=makeQuery(id+"F3.boolean.opBoolean","MERGE",FACE,{"derivedFrom":[makeQuery(id+"F1.opExtrude","CAP_FACE",FACE,{"disambiguationData":[OSD([subQ3,subQ2,subQ1,subQ0])],"isStart":true}),makeQuery(id+"F3.opExtrude","CAP_FACE",FACE,{"disambiguationData":[OSD([subQ3,subQ2,subQ1,subQ0])],"isStart":false})]});}
            var sketch = newSketch(context, id + "F21", { "sketchPlane" : qUnion([Q0])});
            skLineSegment(sketch, "E54", {"start": v(396, -275) * mm, "end": v(218, -275) * mm, "construction": true});
            skLineSegment(sketch, "E55", {"start": v(218, -275) * mm, "end": v(218, 0) * mm, "construction": true});
            skLineSegment(sketch, "E56", {"start": v(0, 0) * mm, "end": v(218, 0) * mm, "construction": true});
            skCircle(sketch, "E57", {"center": v(218, 0) * mm, "radius": 16 * mm});
            skCircle(sketch, "E58.0", {"center": v(218, 0) * mm, "radius": 14 * mm});
            skSolve(sketch);
        }
        {
            var Q0;
            Q0 = qSketchRegion(id + "F21", true);
            extrude(context, id + "F22", {"entities" : qUnion([Q0]), "operationType" : NewBodyOperationType.ADD, "depth" : 15 * mm});
        }
        {
            var Q0;
            {var subQ0=sQuery(id+"F0.wireOp",EDGE,"E2.left");var subQ1=sQuery(id+"F0.wireOp",EDGE,"E2.right");var subQ2=sQuery(id+"F0.wireOp",EDGE,"E2.bottom");var subQ4=sQuery(id+"F0.wireOp",EDGE,"E2.top");Q0=makeQuery(id+"F22.boolean.opBoolean","SPLIT",FACE,{"disambiguationData":[TD([makeQuery(id+"F1.opExtrude","SWEPT_FACE",FACE,{"disambiguationData":[OSD([subQ2])]})])],"derivedFrom":makeQuery(id+"F3.boolean.opBoolean","MERGE",FACE,{"derivedFrom":[makeQuery(id+"F1.opExtrude","CAP_FACE",FACE,{"disambiguationData":[OSD([subQ2,subQ4,subQ0,subQ1])],"isStart":true}),makeQuery(id+"F3.opExtrude","CAP_FACE",FACE,{"disambiguationData":[OSD([subQ2,subQ4,subQ0,subQ1])],"isStart":false})]})});}
            var sketch = newSketch(context, id + "F23", { "sketchPlane" : qUnion([Q0])});
            skLineSegment(sketch, "E59.0.0", {"start": v(397, 275) * mm, "end": v(-397, 275) * mm});
            skLineSegment(sketch, "E59.0.1", {"start": v(-397, 275) * mm, "end": v(-397, 295) * mm});
            skArc(sketch, "E59.0.2", {"start": v(-397, 295) * mm, "mid": v(0, 316) * mm, "end": v(397, 295) * mm});
            skLineSegment(sketch, "E59.0.3", {"start": v(397, 295) * mm, "end": v(397, 275) * mm});
            skSolve(sketch);
        }
        {
            var Q0;
            Q0 = qSketchRegion(id + "F23", true);
            extrude(context, id + "F24", {"entities" : qUnion([Q0]), "operationType" : NewBodyOperationType.ADD, "depth" : 1 * mm});
        }
        {
            var Q0;
            {var subQ0=sQuery(id+"F0.wireOp",EDGE,"E2.left");var subQ1=sQuery(id+"F0.wireOp",EDGE,"E2.right");var subQ2=sQuery(id+"F0.wireOp",EDGE,"E2.bottom");var subQ4=sQuery(id+"F0.wireOp",EDGE,"E2.top");Q0=makeQuery(id+"F22.boolean.opBoolean","SPLIT",FACE,{"disambiguationData":[TD([makeQuery(id+"F1.opExtrude","SWEPT_FACE",FACE,{"disambiguationData":[OSD([subQ2])]})])],"derivedFrom":makeQuery(id+"F3.boolean.opBoolean","MERGE",FACE,{"derivedFrom":[makeQuery(id+"F1.opExtrude","CAP_FACE",FACE,{"disambiguationData":[OSD([subQ2,subQ4,subQ0,subQ1])],"isStart":true}),makeQuery(id+"F3.opExtrude","CAP_FACE",FACE,{"disambiguationData":[OSD([subQ2,subQ4,subQ0,subQ1])],"isStart":false})]})});}
            var sketch = newSketch(context, id + "F25", { "sketchPlane" : qUnion([Q0])});
            skLineSegment(sketch, "E60", {"start": v(0, 275) * mm, "end": v(0, 260) * mm, "construction": true});
            skPoint(sketch, "E60.endSnap0", {"position": v(0, 275) * mm});
            skLineSegment(sketch, "E61", {"start": v(0, 260) * mm, "end": v(200, 260) * mm, "construction": true});
            skLineSegment(sketch, "E62.bottom", {"start": v(200, 260) * mm, "end": v(170, 260) * mm});
            skLineSegment(sketch, "E62.top", {"start": v(200, 275) * mm, "end": v(170, 275) * mm});
            skLineSegment(sketch, "E62.left", {"start": v(200, 260) * mm, "end": v(200, 275) * mm});
            skLineSegment(sketch, "E62.right", {"start": v(170, 260) * mm, "end": v(170, 275) * mm});
            skLineSegment(sketch, "E63.MirrorCS", {"start": v(-170, 260) * mm, "end": v(-170, 275) * mm});
            skLineSegment(sketch, "E64.MirrorCS", {"start": v(0, 260) * mm, "end": v(-200, 260) * mm, "construction": true});
            skLineSegment(sketch, "E65.MirrorCS", {"start": v(-200, 275) * mm, "end": v(-170, 275) * mm});
            skLineSegment(sketch, "E66.MirrorCS", {"start": v(-200, 260) * mm, "end": v(-200, 275) * mm});
            skLineSegment(sketch, "E67.MirrorCS", {"start": v(-200, 260) * mm, "end": v(-170, 260) * mm});
            skSolve(sketch);
        }
        {
            var Q0;
            Q0 = qSketchRegion(id + "F25", true);
            extrude(context, id + "F26", {"entities" : qUnion([Q0]), "operationType" : NewBodyOperationType.REMOVE, "oppositeDirection" : true, "depth" : 10 * mm});
        }
        {
            var Q0;
            Q0=makeQuery(id+"F26.boolean.opBoolean","COPY",EDGE,{"derivedFrom":makeQuery(id+"F26.opExtrude","CAP_EDGE",EDGE,{"disambiguationData":[OSD([sQuery(id+"F25.wireOp",EDGE,"E67.MirrorCS")])],"isStart":false})});
            var Q1;
            Q1=makeQuery(id+"F26.boolean.opBoolean","COPY",EDGE,{"derivedFrom":makeQuery(id+"F26.opExtrude","CAP_EDGE",EDGE,{"disambiguationData":[OSD([sQuery(id+"F25.wireOp",EDGE,"E62.bottom")])],"isStart":false})});
            fillet(context, id + "F27", {"entities" : qUnion([Q0, Q1]), "radius" : 10 * mm, "tangentPropagation" : true, "allowEdgeOverflow" : false});
        }
        {
            var Q0;
            Q0=qCreatedBy(id+"F10.planeOp",FACE);
            var sketch = newSketch(context, id + "F28", { "sketchPlane" : qUnion([Q0])});
            skText(sketch, "E68", { "text": "PAUL Novus300 (RH)", "fontName": "AllertaStencil-Regular.ttf"});
            const initialGuessF28  = {"E68": [-0.397, 0.004, 1, 0, 0.00529]};
            skSetInitialGuess(sketch, initialGuessF28);
            skSolve(sketch);
        }
        {
            var Q0;
            Q0 = qSketchRegion(id + "F28", true);
            extrude(context, id + "F29", {"entities" : qUnion([Q0]), "operationType" : NewBodyOperationType.REMOVE, "oppositeDirection" : true, "depth" : 50 * mm});
        }
    });
